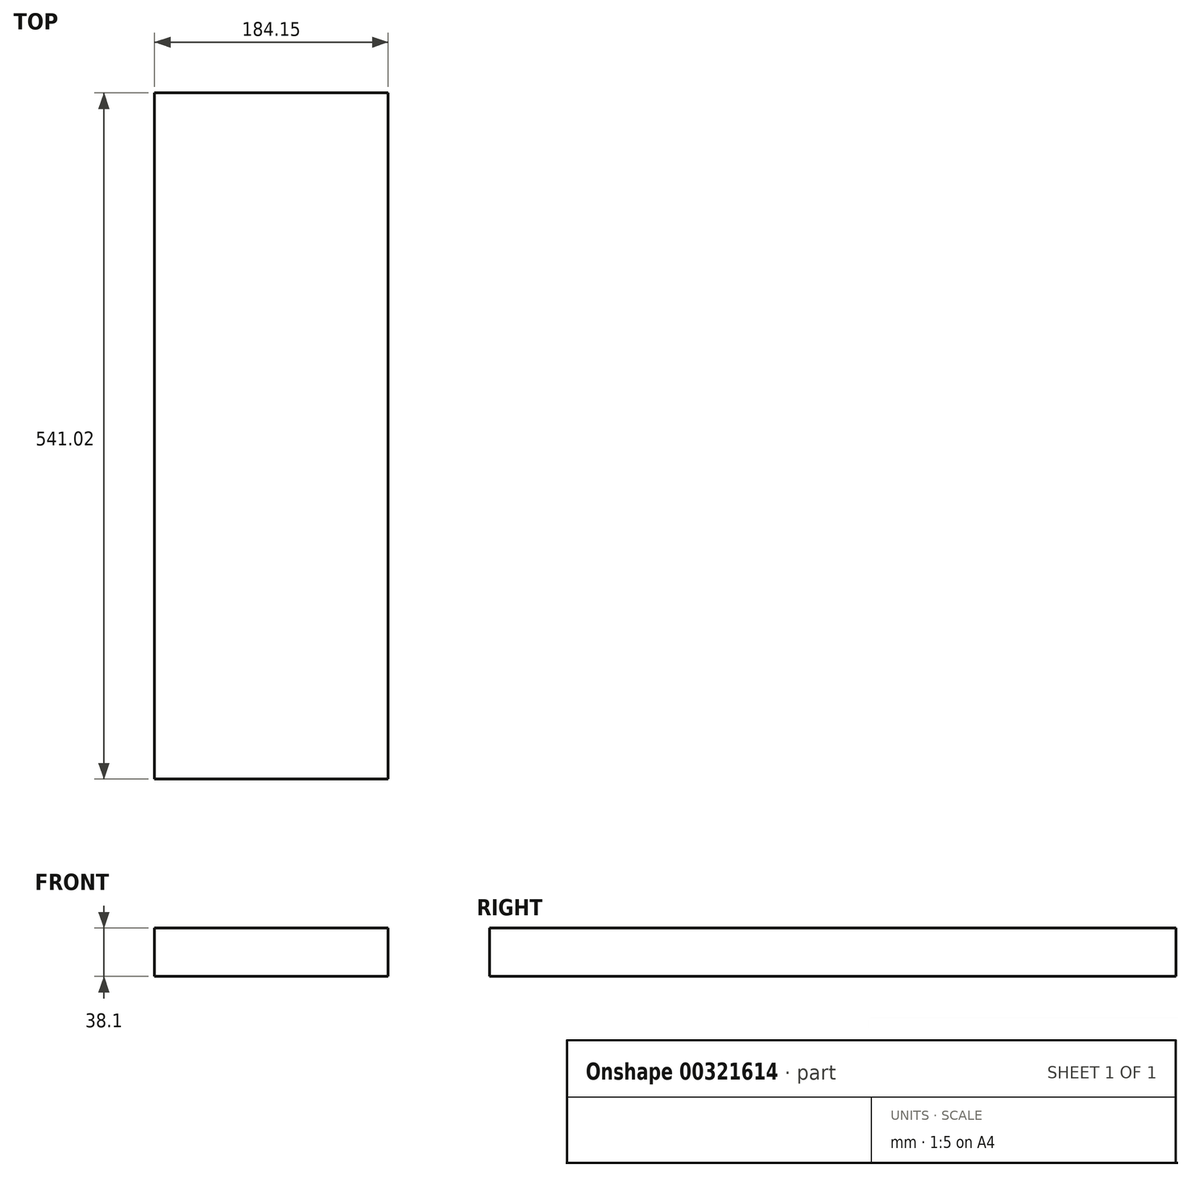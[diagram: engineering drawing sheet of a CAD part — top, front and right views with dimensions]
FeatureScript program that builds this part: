
annotation { "Feature Type Name" : "Feature", "Feature Type Description" : "" }
export const myFeature = defineFeature(function(context is Context, id is Id, definition is map)
    precondition{}
    {
        {
            var Q0;
            Q0=qCreatedBy(makeId("Front.planeOp"),FACE);
            var sketch = newSketch(context, id + "F0", { "sketchPlane" : qUnion([Q0])});
            skLineSegment(sketch, "E0.bottom", {"start": v(-15.81, 6.9) * mm, "end": v(168.34, 6.9) * mm});
            skLineSegment(sketch, "E0.top", {"start": v(-15.81, -31.2) * mm, "end": v(168.34, -31.2) * mm});
            skLineSegment(sketch, "E0.left", {"start": v(-15.81, 6.9) * mm, "end": v(-15.81, -31.2) * mm});
            skLineSegment(sketch, "E0.right", {"start": v(168.34, 6.9) * mm, "end": v(168.34, -31.2) * mm});
            skSolve(sketch);
        }
        {
            var Q0;
            Q0=makeQuery(id+"F0.imprint","IMPRINT",FACE,{"disambiguationData":[TD([[makeQuery(id+"F0.imprint","IMPRINT",EDGE,{"derivedFrom":sQuery(id+"F0.wireOp",EDGE,"E0.bottom")}),-1.0]])]});
            extrude(context, id + "F1", {"entities" : qUnion([Q0]), "depth" : 541.02 * mm});
        }
    });
